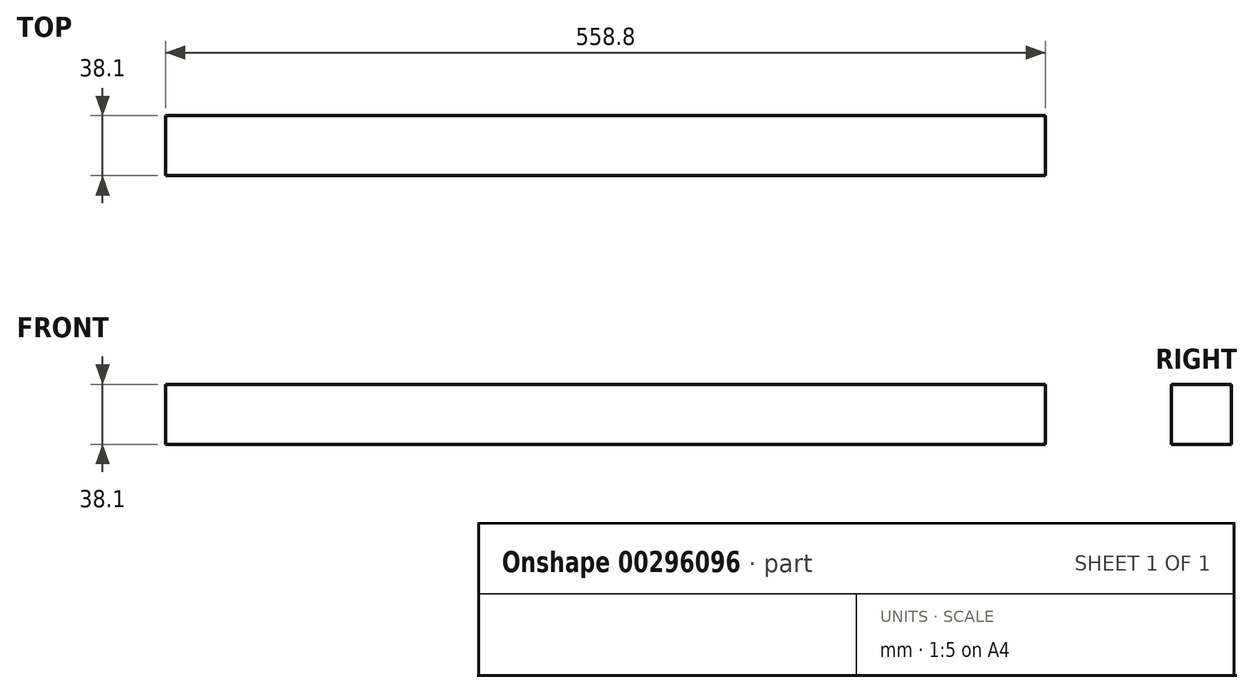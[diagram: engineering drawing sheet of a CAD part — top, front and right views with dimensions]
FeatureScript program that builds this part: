
annotation { "Feature Type Name" : "Feature", "Feature Type Description" : "" }
export const myFeature = defineFeature(function(context is Context, id is Id, definition is map)
    precondition{}
    {
        {
            var Q0;
            Q0=qCreatedBy(makeId("Top.planeOp"),FACE);
            var sketch = newSketch(context, id + "F0", { "sketchPlane" : qUnion([Q0])});
            skLineSegment(sketch, "E0.bottom", {"start": v(279.4, 19.05) * mm, "end": v(-279.4, 19.05) * mm});
            skLineSegment(sketch, "E0.top", {"start": v(279.4, -19.05) * mm, "end": v(-279.4, -19.05) * mm});
            skLineSegment(sketch, "E0.left", {"start": v(279.4, 19.05) * mm, "end": v(279.4, -19.05) * mm});
            skLineSegment(sketch, "E0.right", {"start": v(-279.4, 19.05) * mm, "end": v(-279.4, -19.05) * mm});
            skPoint(sketch, "E0.middle", {"position": v(0, 0) * mm});
            skSolve(sketch);
        }
        {
            var Q0;
            Q0=makeQuery(id+"F0.imprint","IMPRINT",FACE,{"disambiguationData":[TD([[makeQuery(id+"F0.imprint","IMPRINT",EDGE,{"derivedFrom":sQuery(id+"F0.wireOp",EDGE,"E0.bottom")}),1.0]])]});
            extrude(context, id + "F1", {"entities" : qUnion([Q0]), "depth" : 38.1 * mm});
        }
    });
